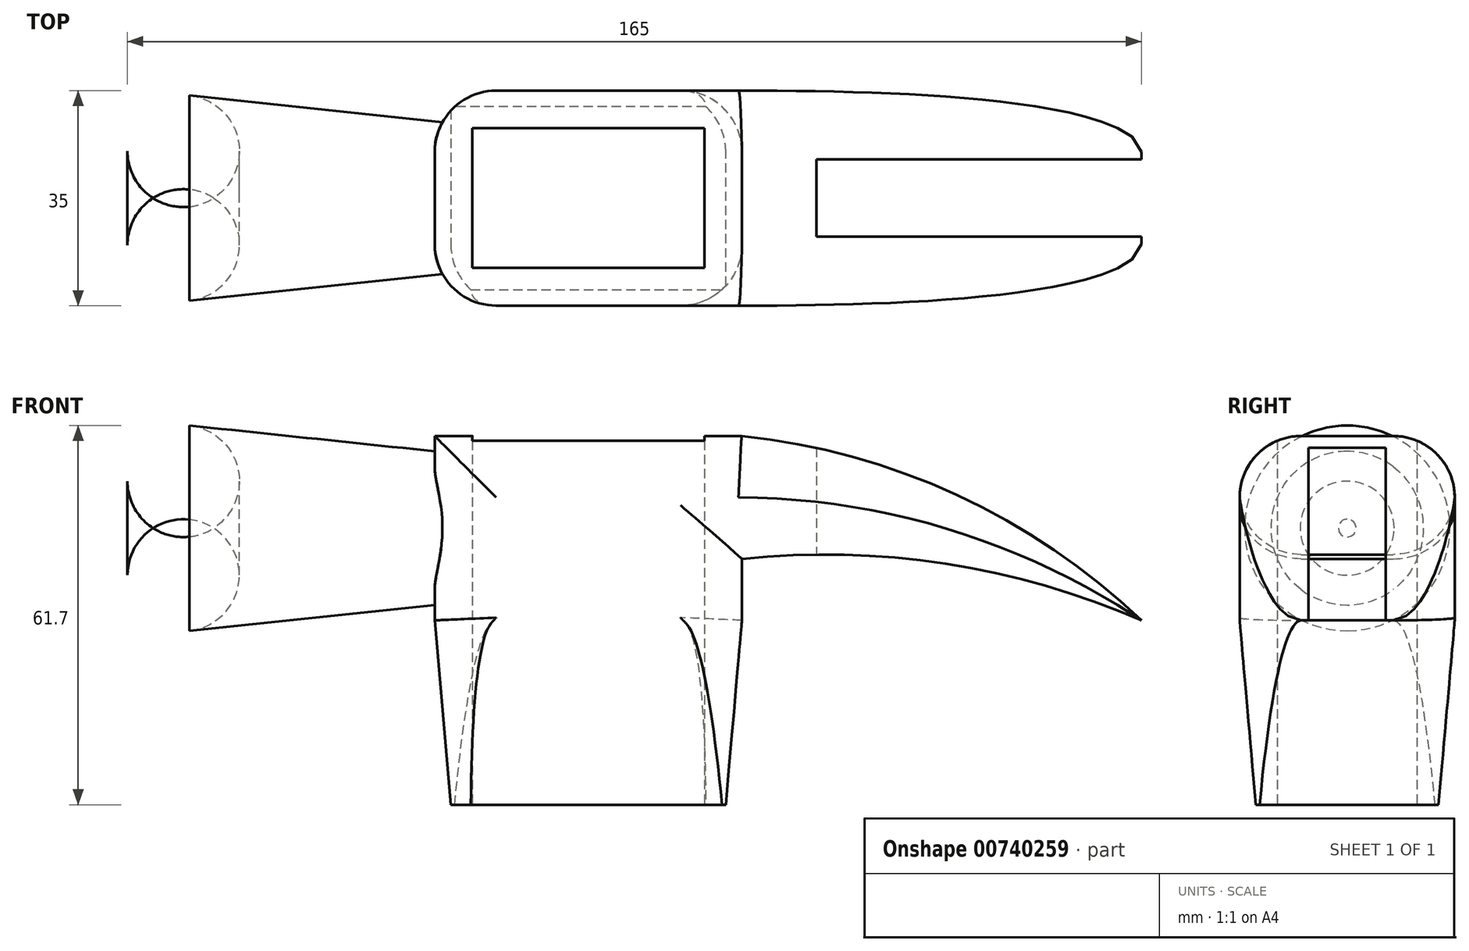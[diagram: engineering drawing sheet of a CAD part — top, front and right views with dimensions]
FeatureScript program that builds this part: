
annotation { "Feature Type Name" : "Feature", "Feature Type Description" : "" }
export const myFeature = defineFeature(function(context is Context, id is Id, definition is map)
    precondition{}
    {
        {
            var Q0;
            Q0=qCreatedBy(makeId("Front.planeOp"),FACE);
            var sketch = newSketch(context, id + "F0", { "sketchPlane" : qUnion([Q0])});
            skLineSegment(sketch, "E0.bottom", {"start": v(0, 0) * mm, "end": v(50, 0) * mm});
            skLineSegment(sketch, "E0.top", {"start": v(0, 30) * mm, "end": v(50, 30) * mm});
            skLineSegment(sketch, "E0.left", {"start": v(0, 0) * mm, "end": v(0, 30) * mm});
            skLineSegment(sketch, "E0.right", {"start": v(50, 0) * mm, "end": v(50, 30) * mm});
            skSolve(sketch);
        }
        {
            var Q0;
            Q0=makeQuery(id+"F0.imprint","IMPRINT",FACE,{"disambiguationData":[TD([[makeQuery(id+"F0.imprint","IMPRINT",EDGE,{"derivedFrom":sQuery(id+"F0.wireOp",EDGE,"E0.bottom")}),1.0]])]});
            extrude(context, id + "F1", {"entities" : qUnion([Q0]), "endBound" : BoundingType.SYMMETRIC, "depth" : 35 * mm, "offsetDistance" : 25 * mm});
        }
        {
            var Q0;
            Q0=makeQuery(id+"F1.opExtrude","SWEPT_FACE",FACE,{"disambiguationData":[OSD([sQuery(id+"F0.wireOp",EDGE,"E0.bottom")])]});
            extrude(context, id + "F2", {"entities" : qUnion([Q0]), "operationType" : NewBodyOperationType.ADD, "depth" : 30 * mm, "offsetDistance" : 25 * mm, "hasDraft" : true, "draftAngle" : 5 * degree, "draftPullDirection" : true});
        }
        {
            var Q0;
            Q0=qCreatedBy(makeId("Right.planeOp"),FACE);
            var sketch = newSketch(context, id + "F3", { "sketchPlane" : qUnion([Q0])});
            skCircle(sketch, "E1", {"center": v(0, 15) * mm, "radius": 12.5 * mm});
            skSolve(sketch);
        }
        {
            var Q0;
            Q0=makeQuery(id+"F3.imprint","IMPRINT",FACE,{"disambiguationData":[TD([[makeQuery(id+"F3.imprint","IMPRINT",EDGE,{"derivedFrom":sQuery(id+"F3.wireOp",EDGE,"E1")}),1.0]])]});
            extrude(context, id + "F4", {"entities" : qUnion([Q0]), "operationType" : NewBodyOperationType.ADD, "oppositeDirection" : true, "depth" : 50 * mm, "offsetDistance" : 25 * mm, "hasDraft" : true, "draftAngle" : 6 * degree});
        }
        {
            var Q0;
            Q0=qCreatedBy(makeId("Front.planeOp"),FACE);
            var sketch = newSketch(context, id + "F5", { "sketchPlane" : qUnion([Q0])});
            skArc(sketch, "E2", {"start": v(115, 0) * mm, "mid": v(84.96, 20.4) * mm, "end": v(49.95, 30) * mm});
            skArc(sketch, "E3", {"start": v(115, 0) * mm, "mid": v(83.13, 9.2) * mm, "end": v(49.97, 10) * mm});
            skLineSegment(sketch, "E4", {"start": v(49.95, 30) * mm, "end": v(49.97, 10) * mm});
            skSolve(sketch);
        }
        {
            var Q0;
            Q0=makeQuery(id+"F5.imprint","IMPRINT",FACE,{"disambiguationData":[TD([[makeQuery(id+"F5.imprint","IMPRINT",EDGE,{"derivedFrom":sQuery(id+"F5.wireOp",EDGE,"E2")}),1.0]])]});
            extrude(context, id + "F6", {"entities" : qUnion([Q0]), "operationType" : NewBodyOperationType.ADD, "endBound" : BoundingType.SYMMETRIC, "depth" : 35 * mm, "offsetDistance" : 25 * mm});
        }
        {
            var Q0;
            Q0=makeQuery(id+"F2.opExtrude","CAP_FACE",FACE,{"disambiguationData":[OSD([sQuery(id+"F0.wireOp",EDGE,"E0.bottom")])],"isStart":false});
            var sketch = newSketch(context, id + "F7", { "sketchPlane" : qUnion([Q0])});
            skLineSegment(sketch, "E5", {"start": v(2.62, 14.88) * mm, "end": v(47.38, 14.88) * mm});
            skLineSegment(sketch, "E6", {"start": v(47.38, 14.88) * mm, "end": v(47.38, -14.88) * mm});
            skLineSegment(sketch, "E7", {"start": v(47.38, -14.88) * mm, "end": v(2.62, -14.88) * mm});
            skLineSegment(sketch, "E8", {"start": v(2.62, -14.88) * mm, "end": v(2.62, 14.88) * mm});
            skLineSegment(sketch, "E9.0", {"start": v(6.12, -11.38) * mm, "end": v(43.88, -11.38) * mm});
            skLineSegment(sketch, "E9.1", {"start": v(6.12, 11.38) * mm, "end": v(6.12, -11.38) * mm});
            skLineSegment(sketch, "E9.2", {"start": v(43.88, 11.38) * mm, "end": v(6.12, 11.38) * mm});
            skLineSegment(sketch, "E9.3", {"start": v(43.88, -11.38) * mm, "end": v(43.88, 11.38) * mm});
            skSolve(sketch);
        }
        {
            var Q0;
            Q0=makeQuery(id+"F7.imprint","IMPRINT",FACE,{"disambiguationData":[TD([[makeQuery(id+"F7.imprint","IMPRINT",EDGE,{"derivedFrom":sQuery(id+"F7.wireOp",EDGE,"E9.0")}),1.0]])]});
            extrude(context, id + "F8", {"entities" : qUnion([Q0]), "operationType" : NewBodyOperationType.REMOVE, "oppositeDirection" : true, "depth" : 81.5 * mm, "offsetDistance" : 25 * mm});
        }
        {
            var Q0;
            Q0=qCreatedBy(makeId("Top.planeOp"),FACE);
            var sketch = newSketch(context, id + "F9", { "sketchPlane" : qUnion([Q0])});
            skLineSegment(sketch, "E10", {"start": v(0, 0) * mm, "end": v(133.7, 0) * mm});
            skLineSegment(sketch, "E11", {"start": v(0, -23.79) * mm, "end": v(0, 23.79) * mm});
            skLineSegment(sketch, "E12.0", {"start": v(62.1, -23.79) * mm, "end": v(62.1, 23.79) * mm});
            skLineSegment(sketch, "E13.0", {"start": v(0, -6.3) * mm, "end": v(133.7, -6.3) * mm});
            skLineSegment(sketch, "E14.0", {"start": v(0, 6.3) * mm, "end": v(133.7, 6.3) * mm});
            skLineSegment(sketch, "E15", {"start": v(62.1, 6.3) * mm, "end": v(62.1, -6.3) * mm});
            skLineSegment(sketch, "E16", {"start": v(62.1, -6.3) * mm, "end": v(133.7, -6.3) * mm});
            skLineSegment(sketch, "E17", {"start": v(133.7, 6.3) * mm, "end": v(62.1, 6.3) * mm});
            skLineSegment(sketch, "E18.bottom", {"start": v(62.1, 6.3) * mm, "end": v(133.7, 6.3) * mm});
            skLineSegment(sketch, "E18.right", {"start": v(133.7, 6.3) * mm, "end": v(133.7, -6.3) * mm});
            skSolve(sketch);
        }
        {
            var Q0;
            {var subQ0=sQuery(id+"F9.wireOp",EDGE,"E12.0");var subQ1=sQuery(id+"F9.wireOp",EDGE,"E10");var subQ2=makeQuery(id+"F9.imprint","INTERSECT",VERTEX,{"derivedFrom":[subQ1,subQ0]});Q0=makeQuery(id+"F9.imprint","IMPRINT",FACE,{"disambiguationData":[TD([[makeQuery(id+"F9.imprint","IMPRINT",EDGE,{"disambiguationData":[TD([[subQ2,-1.0]])],"derivedFrom":subQ1}),1.0]])]});}
            var Q1;
            {var subQ0=sQuery(id+"F9.wireOp",EDGE,"E12.0");var subQ1=sQuery(id+"F9.wireOp",EDGE,"E10");var subQ2=makeQuery(id+"F9.imprint","INTERSECT",VERTEX,{"derivedFrom":[subQ1,subQ0]});Q1=makeQuery(id+"F9.imprint","IMPRINT",FACE,{"disambiguationData":[TD([[makeQuery(id+"F9.imprint","IMPRINT",EDGE,{"disambiguationData":[TD([[subQ2,-1.0]])],"derivedFrom":subQ1}),-1.0]])]});}
            extrude(context, id + "F10", {"entities" : qUnion([Q0, Q1]), "operationType" : NewBodyOperationType.REMOVE, "depth" : 39.5 * mm, "offsetDistance" : 25 * mm});
        }
        {
            var Q0;
            Q0=makeQuery(id+"F6.opExtrude","CAP_EDGE",EDGE,{"disambiguationData":[OSD([sQuery(id+"F5.wireOp",EDGE,"E2")])],"isStart":false});
            var Q1;
            Q1=makeQuery(id+"F6.boolean.opBoolean","MERGE",FACE,{"derivedFrom":[makeQuery(id+"F1.opExtrude","CAP_FACE",FACE,{"disambiguationData":[OSD([sQuery(id+"F0.wireOp",EDGE,"E0.bottom"),sQuery(id+"F0.wireOp",EDGE,"E0.top"),sQuery(id+"F0.wireOp",EDGE,"E0.left"),sQuery(id+"F0.wireOp",EDGE,"E0.right")])],"isStart":false}),makeQuery(id+"F6.opExtrude","CAP_FACE",FACE,{"disambiguationData":[OSD([sQuery(id+"F5.wireOp",EDGE,"E2"),sQuery(id+"F5.wireOp",EDGE,"E3"),sQuery(id+"F5.wireOp",EDGE,"E4")])],"isStart":false})]});
            fillet(context, id + "F11", {"entities" : qUnion([Q0, Q1]), "radius" : 10 * mm, "tangentPropagation" : true, "allowEdgeOverflow" : false});
        }
        {
            var Q0;
            Q0=makeQuery(id+"F6.opExtrude","CAP_EDGE",EDGE,{"disambiguationData":[OSD([sQuery(id+"F5.wireOp",EDGE,"E2")])],"isStart":true});
            var Q1;
            Q1=makeQuery(id+"F6.boolean.opBoolean","MERGE",FACE,{"derivedFrom":[makeQuery(id+"F1.opExtrude","CAP_FACE",FACE,{"disambiguationData":[OSD([sQuery(id+"F0.wireOp",EDGE,"E0.bottom"),sQuery(id+"F0.wireOp",EDGE,"E0.top"),sQuery(id+"F0.wireOp",EDGE,"E0.left"),sQuery(id+"F0.wireOp",EDGE,"E0.right")])],"isStart":true}),makeQuery(id+"F6.opExtrude","CAP_FACE",FACE,{"disambiguationData":[OSD([sQuery(id+"F5.wireOp",EDGE,"E2"),sQuery(id+"F5.wireOp",EDGE,"E3"),sQuery(id+"F5.wireOp",EDGE,"E4")])],"isStart":true})]});
            fillet(context, id + "F12", {"entities" : qUnion([Q0, Q1]), "radius" : 10 * mm, "tangentPropagation" : true, "allowEdgeOverflow" : false});
        }
        {
            var Q0;
            Q0=makeQuery(id+"F4.opExtrude","CAP_EDGE",EDGE,{"disambiguationData":[OSD([sQuery(id+"F3.wireOp",EDGE,"E1")])],"isStart":false});
            fillet(context, id + "F13", {"entities" : qUnion([Q0]), "radius" : 9.1 * mm, "tangentPropagation" : true, "allowEdgeOverflow" : false});
        }
    });
